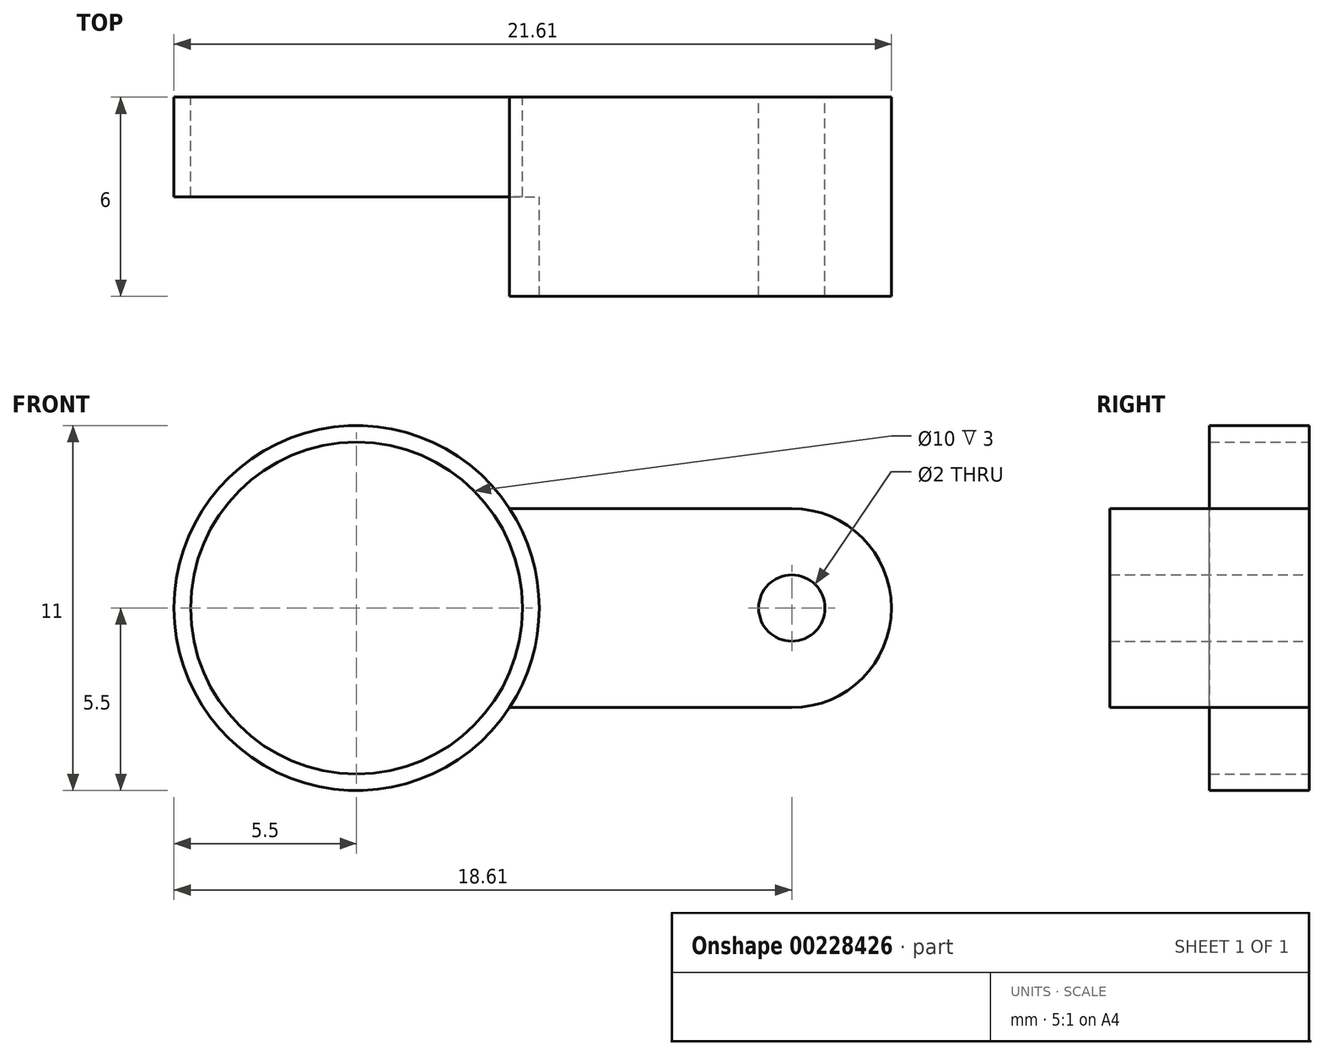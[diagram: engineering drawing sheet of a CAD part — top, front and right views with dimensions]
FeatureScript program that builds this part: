
annotation { "Feature Type Name" : "Feature", "Feature Type Description" : "" }
export const myFeature = defineFeature(function(context is Context, id is Id, definition is map)
    precondition{}
    {
        {
            var Q0;
            Q0=qCreatedBy(makeId("Front.planeOp"),FACE);
            var sketch = newSketch(context, id + "F0", { "sketchPlane" : qUnion([Q0])});
            skCircle(sketch, "E0", {"center": v(0, 0) * mm, "radius": 5.5 * mm});
            skLineSegment(sketch, "E1.bottom", {"start": v(4.6, 3) * mm, "end": v(13.1, 3) * mm});
            skLineSegment(sketch, "E1.top", {"start": v(4.6, -3) * mm, "end": v(13.1, -3) * mm});
            skLineSegment(sketch, "E1.right", {"start": v(13.1, 3) * mm, "end": v(13.1, -3) * mm});
            skArc(sketch, "E2", {"start": v(13.1, -3) * mm, "mid": v(16.1, 0) * mm, "end": v(13.1, 3) * mm});
            skCircle(sketch, "E3", {"center": v(13.1, 0) * mm, "radius": 1 * mm});
            skCircle(sketch, "E4", {"center": v(0, 0) * mm, "radius": 5 * mm});
            skSolve(sketch);
        }
        {
            var Q0;
            Q0=makeQuery(id+"F0.imprint","IMPRINT",FACE,{"disambiguationData":[TD([[makeQuery(id+"F0.imprint","IMPRINT",EDGE,{"derivedFrom":sQuery(id+"F0.wireOp",EDGE,"E4")}),-1.0]])]});
            var Q1;
            {var subQ2=sQuery(id+"F0.wireOp",EDGE,"E1.bottom");Q1=makeQuery(id+"F0.imprint","IMPRINT",FACE,{"disambiguationData":[TD([[makeQuery(id+"F0.imprint","IMPRINT",EDGE,{"derivedFrom":subQ2}),-1.0]])]});}
            var Q2;
            {var subQ0=sQuery(id+"F0.wireOp",EDGE,"E2");Q2=makeQuery(id+"F0.imprint","IMPRINT",FACE,{"disambiguationData":[TD([[makeQuery(id+"F0.imprint","IMPRINT",EDGE,{"derivedFrom":subQ0}),1.0]])]});}
            extrude(context, id + "F1", {"entities" : qUnion([Q0, Q1, Q2]), "depth" : 3 * mm});
        }
        {
            var Q0;
            {var subQ0=sQuery(id+"F0.wireOp",EDGE,"E3");var subQ1=sQuery(id+"F0.wireOp",EDGE,"E1.right");var subQ2=makeQuery(id+"F0.imprint","INTERSECT",VERTEX,{"disambiguationData":[OD(0.0)],"derivedFrom":[subQ1,subQ0]});Q0=makeQuery(id+"F0.imprint","IMPRINT",FACE,{"disambiguationData":[TD([[makeQuery(id+"F0.imprint","IMPRINT",EDGE,{"disambiguationData":[TD([[subQ2,-1.0]])],"derivedFrom":subQ1}),-1.0]])]});}
            var Q1;
            {var subQ0=sQuery(id+"F0.wireOp",EDGE,"E3");var subQ1=sQuery(id+"F0.wireOp",EDGE,"E1.right");var subQ2=makeQuery(id+"F0.imprint","INTERSECT",VERTEX,{"disambiguationData":[OD(0.0)],"derivedFrom":[subQ1,subQ0]});Q1=makeQuery(id+"F0.imprint","IMPRINT",FACE,{"disambiguationData":[TD([[makeQuery(id+"F0.imprint","IMPRINT",EDGE,{"disambiguationData":[TD([[subQ2,-1.0]])],"derivedFrom":subQ1}),1.0]])]});}
            extrude(context, id + "F2", {"entities" : qUnion([Q0, Q1]), "operationType" : NewBodyOperationType.ADD, "depth" : 6 * mm});
        }
    });
